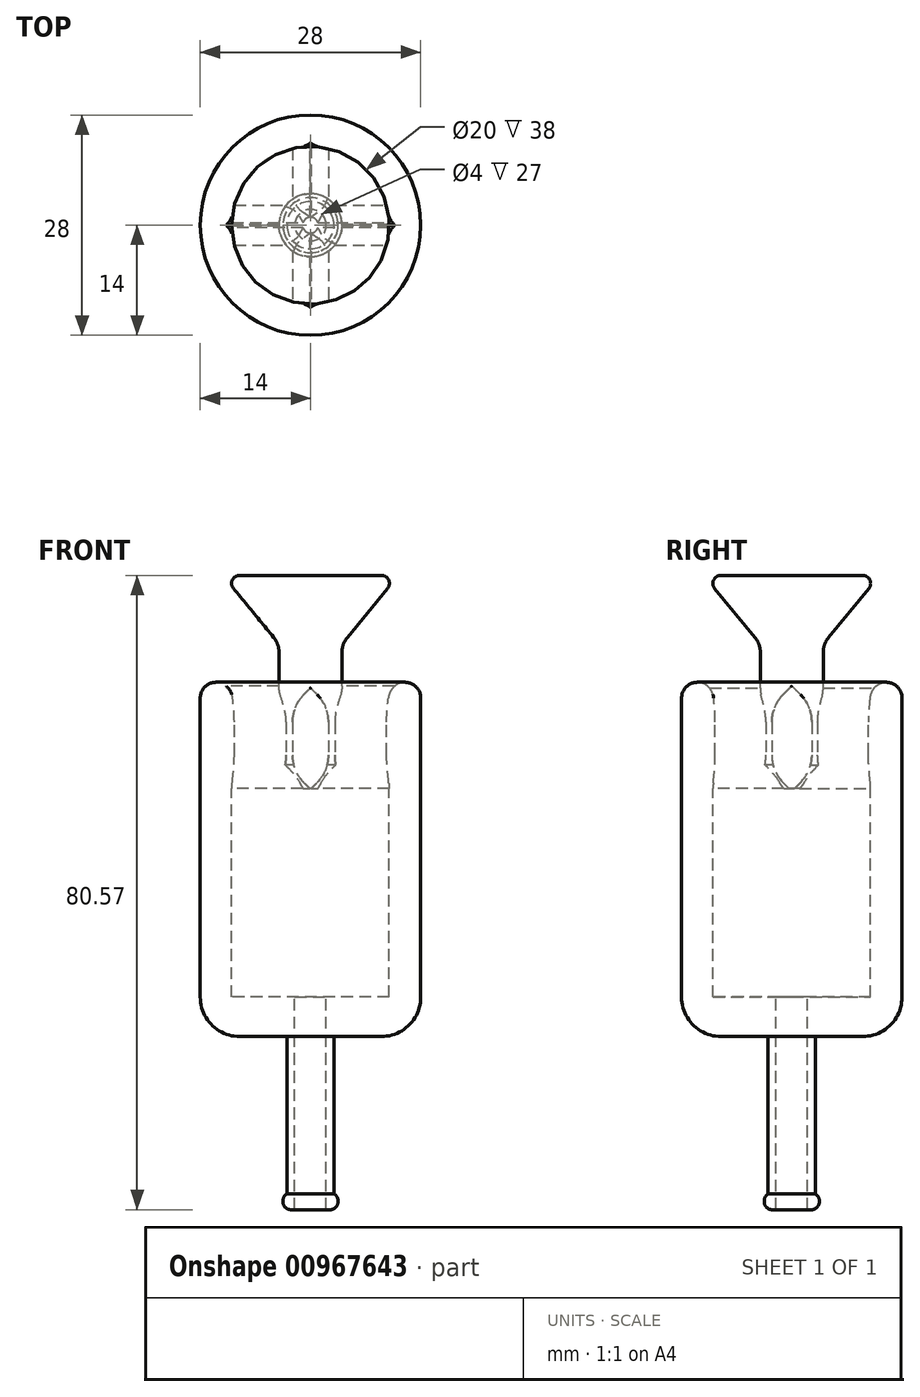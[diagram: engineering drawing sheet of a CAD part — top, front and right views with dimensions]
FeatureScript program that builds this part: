
annotation { "Feature Type Name" : "Feature", "Feature Type Description" : "" }
export const myFeature = defineFeature(function(context is Context, id is Id, definition is map)
    precondition{}
    {
        {
            var Q0;
            Q0=qCreatedBy(makeId("Front.planeOp"),FACE);
            var sketch = newSketch(context, id + "F0", { "sketchPlane" : qUnion([Q0])});
            skLineSegment(sketch, "E0", {"start": v(0, 0) * mm, "end": v(-11.14, 13.57) * mm});
            skLineSegment(sketch, "E1", {"start": v(-11.14, 13.57) * mm, "end": v(0, 13.57) * mm});
            skLineSegment(sketch, "E2", {"start": v(0, 13.57) * mm, "end": v(0, 0) * mm});
            skLineSegment(sketch, "E3", {"start": v(0, 0) * mm, "end": v(-5.28, 0) * mm});
            skLineSegment(sketch, "E4", {"start": v(-5.28, 0) * mm, "end": v(-5.28, -11.56) * mm});
            skLineSegment(sketch, "E5", {"start": v(-5.28, -11.56) * mm, "end": v(0, -11.56) * mm});
            skLineSegment(sketch, "E6", {"start": v(0, -11.56) * mm, "end": v(0, 0) * mm});
            skSolve(sketch);
        }
        {
            var Q0;
            Q0=makeQuery(id+"F0.imprint","IMPRINT",FACE,{"disambiguationData":[TD([[makeQuery(id+"F0.imprint","IMPRINT",EDGE,{"derivedFrom":sQuery(id+"F0.wireOp",EDGE,"E0")}),-1.0]])]});
            var Q1;
            Q1=sQuery(id+"F0.wireOp",EDGE,"E2");
            revolve(context, id + "F1", {"surfaceOperationType" : NewSurfaceOperationType.NEW, "entities" : qUnion([Q0]), "axis" : qUnion([Q1]), "revolveType" : RevolveType.FULL});
        }
        {
            var Q0;
            Q0=qCreatedBy(makeId("Top.planeOp"),FACE);
            var sketch = newSketch(context, id + "F2", { "sketchPlane" : qUnion([Q0])});
            skCircle(sketch, "E7", {"center": v(0, 0) * mm, "radius": 14 * mm});
            skCircle(sketch, "E8", {"center": v(0, 0) * mm, "radius": 10 * mm});
            skCircle(sketch, "E9", {"center": v(0, 0) * mm, "radius": 4 * mm});
            skSolve(sketch);
        }
        {
            var Q0;
            Q0=makeQuery(id+"F2.imprint","IMPRINT",FACE,{"disambiguationData":[TD([[makeQuery(id+"F2.imprint","IMPRINT",EDGE,{"derivedFrom":sQuery(id+"F2.wireOp",EDGE,"E9")}),1.0]])]});
            extrude(context, id + "F3", {"entities" : qUnion([Q0]), "operationType" : NewBodyOperationType.ADD, "endBound" : BoundingType.SYMMETRIC, "oppositeDirection" : true, "depth" : 27 * mm, "offsetDistance" : 25 * mm});
        }
        {
            var Q0;
            Q0=makeQuery(id+"F2.imprint","IMPRINT",FACE,{"disambiguationData":[TD([[makeQuery(id+"F2.imprint","IMPRINT",EDGE,{"derivedFrom":sQuery(id+"F2.wireOp",EDGE,"E7")}),1.0]])]});
            extrude(context, id + "F4", {"entities" : qUnion([Q0]), "depth" : -40 * mm, "offsetDistance" : 25 * mm});
        }
        {
            var Q0;
            Q0=makeQuery(id+"F3.opExtrude","CAP_FACE",FACE,{"disambiguationData":[OSD([sQuery(id+"F2.wireOp",EDGE,"E9")])],"isStart":false});
            var sketch = newSketch(context, id + "F5", { "sketchPlane" : qUnion([Q0])});
            skLineSegment(sketch, "E10.bottom", {"start": v(2.28, -13) * mm, "end": v(-2.28, -13) * mm});
            skLineSegment(sketch, "E10.top", {"start": v(2.28, 13) * mm, "end": v(-2.28, 13) * mm});
            skLineSegment(sketch, "E10.left", {"start": v(2.28, -13) * mm, "end": v(2.28, 13) * mm});
            skLineSegment(sketch, "E10.right", {"start": v(-2.28, -13) * mm, "end": v(-2.28, 13) * mm});
            skPoint(sketch, "E10.middle", {"position": v(0, 0) * mm});
            skLineSegment(sketch, "E11.bottom", {"start": v(-13.08, 2.54) * mm, "end": v(13.08, 2.54) * mm});
            skLineSegment(sketch, "E11.top", {"start": v(-13.08, -2.54) * mm, "end": v(13.08, -2.54) * mm});
            skLineSegment(sketch, "E11.left", {"start": v(-13.08, 2.54) * mm, "end": v(-13.08, -2.54) * mm});
            skLineSegment(sketch, "E11.right", {"start": v(13.08, 2.54) * mm, "end": v(13.08, -2.54) * mm});
            skSolve(sketch);
        }
        {
            var Q0;
            {var subQ0=sQuery(id+"F5.wireOp",EDGE,"E11.left");Q0=makeQuery(id+"F5.imprint","IMPRINT",FACE,{"disambiguationData":[TD([[makeQuery(id+"F5.imprint","IMPRINT",EDGE,{"derivedFrom":subQ0}),1.0]])]});}
            var Q1;
            {var subQ0=sQuery(id+"F5.wireOp",EDGE,"E11.right");Q1=makeQuery(id+"F5.imprint","IMPRINT",FACE,{"disambiguationData":[TD([[makeQuery(id+"F5.imprint","IMPRINT",EDGE,{"derivedFrom":subQ0}),-1.0]])]});}
            var Q2;
            {var subQ0=sQuery(id+"F5.wireOp",EDGE,"E10.top");Q2=makeQuery(id+"F5.imprint","IMPRINT",FACE,{"disambiguationData":[TD([[makeQuery(id+"F5.imprint","IMPRINT",EDGE,{"derivedFrom":subQ0}),1.0]])]});}
            var Q3;
            {var subQ0=sQuery(id+"F5.wireOp",EDGE,"E10.bottom");Q3=makeQuery(id+"F5.imprint","IMPRINT",FACE,{"disambiguationData":[TD([[makeQuery(id+"F5.imprint","IMPRINT",EDGE,{"derivedFrom":subQ0}),-1.0]])]});}
            extrude(context, id + "F6", {"entities" : qUnion([Q0, Q1, Q2, Q3]), "operationType" : NewBodyOperationType.ADD, "depth" : -13 * mm, "offsetDistance" : 25 * mm});
        }
        {
            var Q0;
            {var subQ0=sQuery(id+"F5.wireOp",EDGE,"E11.bottom");Q0=makeQuery(id+"F6.opExtrude","CAP_EDGE",EDGE,{"disambiguationData":[OSD([subQ0]),TDD([makeQuery(id+"F5.imprint","IMPRINT",EDGE,{"disambiguationData":[TD([[makeQuery(id+"F5.imprint","INTERSECT",VERTEX,{"derivedFrom":[subQ0,sQuery(id+"F5.wireOp",EDGE,"E11.left")]}),-1.0]])],"derivedFrom":subQ0})])],"isStart":true});}
            var Q1;
            {var subQ0=sQuery(id+"F5.wireOp",EDGE,"E11.top");Q1=makeQuery(id+"F6.opExtrude","CAP_EDGE",EDGE,{"disambiguationData":[OSD([subQ0]),TDD([makeQuery(id+"F5.imprint","IMPRINT",EDGE,{"disambiguationData":[TD([[makeQuery(id+"F5.imprint","INTERSECT",VERTEX,{"derivedFrom":[subQ0,sQuery(id+"F5.wireOp",EDGE,"E11.right")]}),1.0]])],"derivedFrom":subQ0})])],"isStart":true});}
            var Q2;
            {var subQ0=sQuery(id+"F5.wireOp",EDGE,"E10.left");Q2=makeQuery(id+"F6.opExtrude","CAP_EDGE",EDGE,{"disambiguationData":[OSD([subQ0]),TDD([makeQuery(id+"F5.imprint","IMPRINT",EDGE,{"disambiguationData":[TD([[makeQuery(id+"F5.imprint","INTERSECT",VERTEX,{"derivedFrom":[sQuery(id+"F5.wireOp",EDGE,"E10.top"),subQ0]}),1.0]])],"derivedFrom":subQ0})])],"isStart":true});}
            var Q3;
            {var subQ0=sQuery(id+"F5.wireOp",EDGE,"E10.right");Q3=makeQuery(id+"F6.opExtrude","CAP_EDGE",EDGE,{"disambiguationData":[OSD([subQ0]),TDD([makeQuery(id+"F5.imprint","IMPRINT",EDGE,{"disambiguationData":[TD([[makeQuery(id+"F5.imprint","INTERSECT",VERTEX,{"derivedFrom":[sQuery(id+"F5.wireOp",EDGE,"E10.bottom"),subQ0]}),-1.0]])],"derivedFrom":subQ0})])],"isStart":true});}
            var Q4;
            {var subQ0=sQuery(id+"F5.wireOp",EDGE,"E11.top");Q4=makeQuery(id+"F6.opExtrude","CAP_EDGE",EDGE,{"disambiguationData":[OSD([subQ0]),TDD([makeQuery(id+"F5.imprint","IMPRINT",EDGE,{"disambiguationData":[TD([[makeQuery(id+"F5.imprint","INTERSECT",VERTEX,{"derivedFrom":[subQ0,sQuery(id+"F5.wireOp",EDGE,"E11.left")]}),-1.0]])],"derivedFrom":subQ0})])],"isStart":true});}
            var Q5;
            {var subQ0=sQuery(id+"F5.wireOp",EDGE,"E11.bottom");Q5=makeQuery(id+"F6.opExtrude","CAP_EDGE",EDGE,{"disambiguationData":[OSD([subQ0]),TDD([makeQuery(id+"F5.imprint","IMPRINT",EDGE,{"disambiguationData":[TD([[makeQuery(id+"F5.imprint","INTERSECT",VERTEX,{"derivedFrom":[subQ0,sQuery(id+"F5.wireOp",EDGE,"E11.right")]}),1.0]])],"derivedFrom":subQ0})])],"isStart":true});}
            var Q6;
            {var subQ0=sQuery(id+"F5.wireOp",EDGE,"E10.right");Q6=makeQuery(id+"F6.opExtrude","CAP_EDGE",EDGE,{"disambiguationData":[OSD([subQ0]),TDD([makeQuery(id+"F5.imprint","IMPRINT",EDGE,{"disambiguationData":[TD([[makeQuery(id+"F5.imprint","INTERSECT",VERTEX,{"derivedFrom":[sQuery(id+"F5.wireOp",EDGE,"E10.top"),subQ0]}),1.0]])],"derivedFrom":subQ0})])],"isStart":true});}
            var Q7;
            {var subQ0=sQuery(id+"F5.wireOp",EDGE,"E10.left");Q7=makeQuery(id+"F6.opExtrude","CAP_EDGE",EDGE,{"disambiguationData":[OSD([subQ0]),TDD([makeQuery(id+"F5.imprint","IMPRINT",EDGE,{"disambiguationData":[TD([[makeQuery(id+"F5.imprint","INTERSECT",VERTEX,{"derivedFrom":[sQuery(id+"F5.wireOp",EDGE,"E10.bottom"),subQ0]}),-1.0]])],"derivedFrom":subQ0})])],"isStart":true});}
            chamfer(context, id + "F7", {"entities" : qUnion([Q0, Q1, Q2, Q3, Q4, Q5, Q6, Q7]), "width" : 2.2 * mm, "tangentPropagation" : true});
        }
        {
            var Q0;
            {var subQ0=sQuery(id+"F5.wireOp",EDGE,"E11.bottom");Q0=makeQuery(id+"F6.opExtrude","CAP_EDGE",EDGE,{"disambiguationData":[OSD([subQ0]),TDD([makeQuery(id+"F5.imprint","IMPRINT",EDGE,{"disambiguationData":[TD([[makeQuery(id+"F5.imprint","INTERSECT",VERTEX,{"derivedFrom":[subQ0,sQuery(id+"F5.wireOp",EDGE,"E11.left")]}),-1.0]])],"derivedFrom":subQ0})])],"isStart":false});}
            var Q1;
            {var subQ0=sQuery(id+"F5.wireOp",EDGE,"E11.top");Q1=makeQuery(id+"F6.opExtrude","CAP_EDGE",EDGE,{"disambiguationData":[OSD([subQ0]),TDD([makeQuery(id+"F5.imprint","IMPRINT",EDGE,{"disambiguationData":[TD([[makeQuery(id+"F5.imprint","INTERSECT",VERTEX,{"derivedFrom":[subQ0,sQuery(id+"F5.wireOp",EDGE,"E11.left")]}),-1.0]])],"derivedFrom":subQ0})])],"isStart":false});}
            var Q2;
            {var subQ0=sQuery(id+"F5.wireOp",EDGE,"E10.right");Q2=makeQuery(id+"F6.opExtrude","CAP_EDGE",EDGE,{"disambiguationData":[OSD([subQ0]),TDD([makeQuery(id+"F5.imprint","IMPRINT",EDGE,{"disambiguationData":[TD([[makeQuery(id+"F5.imprint","INTERSECT",VERTEX,{"derivedFrom":[sQuery(id+"F5.wireOp",EDGE,"E10.bottom"),subQ0]}),-1.0]])],"derivedFrom":subQ0})])],"isStart":false});}
            var Q3;
            {var subQ0=sQuery(id+"F5.wireOp",EDGE,"E10.left");Q3=makeQuery(id+"F6.opExtrude","CAP_EDGE",EDGE,{"disambiguationData":[OSD([subQ0]),TDD([makeQuery(id+"F5.imprint","IMPRINT",EDGE,{"disambiguationData":[TD([[makeQuery(id+"F5.imprint","INTERSECT",VERTEX,{"derivedFrom":[sQuery(id+"F5.wireOp",EDGE,"E10.bottom"),subQ0]}),-1.0]])],"derivedFrom":subQ0})])],"isStart":false});}
            var Q4;
            {var subQ0=sQuery(id+"F5.wireOp",EDGE,"E11.bottom");Q4=makeQuery(id+"F6.opExtrude","CAP_EDGE",EDGE,{"disambiguationData":[OSD([subQ0]),TDD([makeQuery(id+"F5.imprint","IMPRINT",EDGE,{"disambiguationData":[TD([[makeQuery(id+"F5.imprint","INTERSECT",VERTEX,{"derivedFrom":[subQ0,sQuery(id+"F5.wireOp",EDGE,"E11.right")]}),1.0]])],"derivedFrom":subQ0})])],"isStart":false});}
            var Q5;
            {var subQ0=sQuery(id+"F5.wireOp",EDGE,"E11.top");Q5=makeQuery(id+"F6.opExtrude","CAP_EDGE",EDGE,{"disambiguationData":[OSD([subQ0]),TDD([makeQuery(id+"F5.imprint","IMPRINT",EDGE,{"disambiguationData":[TD([[makeQuery(id+"F5.imprint","INTERSECT",VERTEX,{"derivedFrom":[subQ0,sQuery(id+"F5.wireOp",EDGE,"E11.right")]}),1.0]])],"derivedFrom":subQ0})])],"isStart":false});}
            var Q6;
            {var subQ0=sQuery(id+"F5.wireOp",EDGE,"E10.left");Q6=makeQuery(id+"F6.opExtrude","CAP_EDGE",EDGE,{"disambiguationData":[OSD([subQ0]),TDD([makeQuery(id+"F5.imprint","IMPRINT",EDGE,{"disambiguationData":[TD([[makeQuery(id+"F5.imprint","INTERSECT",VERTEX,{"derivedFrom":[sQuery(id+"F5.wireOp",EDGE,"E10.top"),subQ0]}),1.0]])],"derivedFrom":subQ0})])],"isStart":false});}
            var Q7;
            {var subQ0=sQuery(id+"F5.wireOp",EDGE,"E10.right");Q7=makeQuery(id+"F6.opExtrude","CAP_EDGE",EDGE,{"disambiguationData":[OSD([subQ0]),TDD([makeQuery(id+"F5.imprint","IMPRINT",EDGE,{"disambiguationData":[TD([[makeQuery(id+"F5.imprint","INTERSECT",VERTEX,{"derivedFrom":[sQuery(id+"F5.wireOp",EDGE,"E10.top"),subQ0]}),1.0]])],"derivedFrom":subQ0})])],"isStart":false});}
            chamfer(context, id + "F8", {"entities" : qUnion([Q0, Q1, Q2, Q3, Q4, Q5, Q6, Q7]), "width" : 2.5 * mm, "tangentPropagation" : true});
        }
        {
            var Q0;
            {var subQ0=sQuery(id+"F5.wireOp",EDGE,"E10.right");var subQ1=makeQuery(id+"F5.imprint","IMPRINT",EDGE,{"disambiguationData":[TD([[makeQuery(id+"F5.imprint","INTERSECT",VERTEX,{"derivedFrom":[sQuery(id+"F5.wireOp",EDGE,"E10.top"),subQ0]}),1.0]])],"derivedFrom":subQ0});Q0=makeQuery(id+"F7.opChamfer","BLEND_EDGE",EDGE,{"blendedFrom":[makeQuery(id+"F6.opExtrude","CAP_EDGE",EDGE,{"disambiguationData":[OSD([subQ0]),TDD([subQ1])],"isStart":true}),makeQuery(id+"F6.opExtrude","SWEPT_FACE",FACE,{"disambiguationData":[OSD([subQ0]),TDD([subQ1])]})],"blendedInto":[makeQuery(id+"F6.opExtrude","SWEPT_FACE",FACE,{"disambiguationData":[OSD([subQ0]),TDD([subQ1])]})]});}
            var Q1;
            {var subQ0=sQuery(id+"F5.wireOp",EDGE,"E10.left");var subQ1=makeQuery(id+"F5.imprint","IMPRINT",EDGE,{"disambiguationData":[TD([[makeQuery(id+"F5.imprint","INTERSECT",VERTEX,{"derivedFrom":[sQuery(id+"F5.wireOp",EDGE,"E10.top"),subQ0]}),1.0]])],"derivedFrom":subQ0});Q1=makeQuery(id+"F7.opChamfer","BLEND_EDGE",EDGE,{"blendedFrom":[makeQuery(id+"F6.opExtrude","CAP_EDGE",EDGE,{"disambiguationData":[OSD([subQ0]),TDD([subQ1])],"isStart":true}),makeQuery(id+"F6.opExtrude","SWEPT_FACE",FACE,{"disambiguationData":[OSD([subQ0]),TDD([subQ1])]})],"blendedInto":[makeQuery(id+"F6.opExtrude","SWEPT_FACE",FACE,{"disambiguationData":[OSD([subQ0]),TDD([subQ1])]})]});}
            var Q2;
            {var subQ0=sQuery(id+"F5.wireOp",EDGE,"E11.bottom");var subQ1=makeQuery(id+"F5.imprint","IMPRINT",EDGE,{"disambiguationData":[TD([[makeQuery(id+"F5.imprint","INTERSECT",VERTEX,{"derivedFrom":[subQ0,sQuery(id+"F5.wireOp",EDGE,"E11.right")]}),1.0]])],"derivedFrom":subQ0});Q2=makeQuery(id+"F7.opChamfer","BLEND_EDGE",EDGE,{"blendedFrom":[makeQuery(id+"F6.opExtrude","CAP_EDGE",EDGE,{"disambiguationData":[OSD([subQ0]),TDD([subQ1])],"isStart":true}),makeQuery(id+"F6.opExtrude","SWEPT_FACE",FACE,{"disambiguationData":[OSD([subQ0]),TDD([subQ1])]})],"blendedInto":[makeQuery(id+"F6.opExtrude","SWEPT_FACE",FACE,{"disambiguationData":[OSD([subQ0]),TDD([subQ1])]})]});}
            var Q3;
            {var subQ0=sQuery(id+"F5.wireOp",EDGE,"E11.bottom");var subQ1=makeQuery(id+"F5.imprint","IMPRINT",EDGE,{"disambiguationData":[TD([[makeQuery(id+"F5.imprint","INTERSECT",VERTEX,{"derivedFrom":[subQ0,sQuery(id+"F5.wireOp",EDGE,"E11.left")]}),-1.0]])],"derivedFrom":subQ0});Q3=makeQuery(id+"F7.opChamfer","BLEND_EDGE",EDGE,{"blendedFrom":[makeQuery(id+"F6.opExtrude","CAP_EDGE",EDGE,{"disambiguationData":[OSD([subQ0]),TDD([subQ1])],"isStart":true}),makeQuery(id+"F6.opExtrude","SWEPT_FACE",FACE,{"disambiguationData":[OSD([subQ0]),TDD([subQ1])]})],"blendedInto":[makeQuery(id+"F6.opExtrude","SWEPT_FACE",FACE,{"disambiguationData":[OSD([subQ0]),TDD([subQ1])]})]});}
            var Q4;
            {var subQ0=sQuery(id+"F5.wireOp",EDGE,"E11.top");var subQ1=makeQuery(id+"F5.imprint","IMPRINT",EDGE,{"disambiguationData":[TD([[makeQuery(id+"F5.imprint","INTERSECT",VERTEX,{"derivedFrom":[subQ0,sQuery(id+"F5.wireOp",EDGE,"E11.left")]}),-1.0]])],"derivedFrom":subQ0});Q4=makeQuery(id+"F7.opChamfer","BLEND_EDGE",EDGE,{"blendedFrom":[makeQuery(id+"F6.opExtrude","CAP_EDGE",EDGE,{"disambiguationData":[OSD([subQ0]),TDD([subQ1])],"isStart":true}),makeQuery(id+"F6.opExtrude","SWEPT_FACE",FACE,{"disambiguationData":[OSD([subQ0]),TDD([subQ1])]})],"blendedInto":[makeQuery(id+"F6.opExtrude","SWEPT_FACE",FACE,{"disambiguationData":[OSD([subQ0]),TDD([subQ1])]})]});}
            var Q5;
            {var subQ0=sQuery(id+"F5.wireOp",EDGE,"E11.top");var subQ1=makeQuery(id+"F5.imprint","IMPRINT",EDGE,{"disambiguationData":[TD([[makeQuery(id+"F5.imprint","INTERSECT",VERTEX,{"derivedFrom":[subQ0,sQuery(id+"F5.wireOp",EDGE,"E11.right")]}),1.0]])],"derivedFrom":subQ0});Q5=makeQuery(id+"F7.opChamfer","BLEND_EDGE",EDGE,{"blendedFrom":[makeQuery(id+"F6.opExtrude","CAP_EDGE",EDGE,{"disambiguationData":[OSD([subQ0]),TDD([subQ1])],"isStart":true}),makeQuery(id+"F6.opExtrude","SWEPT_FACE",FACE,{"disambiguationData":[OSD([subQ0]),TDD([subQ1])]})],"blendedInto":[makeQuery(id+"F6.opExtrude","SWEPT_FACE",FACE,{"disambiguationData":[OSD([subQ0]),TDD([subQ1])]})]});}
            var Q6;
            {var subQ0=sQuery(id+"F5.wireOp",EDGE,"E10.right");var subQ1=makeQuery(id+"F5.imprint","IMPRINT",EDGE,{"disambiguationData":[TD([[makeQuery(id+"F5.imprint","INTERSECT",VERTEX,{"derivedFrom":[sQuery(id+"F5.wireOp",EDGE,"E10.bottom"),subQ0]}),-1.0]])],"derivedFrom":subQ0});Q6=makeQuery(id+"F7.opChamfer","BLEND_EDGE",EDGE,{"blendedFrom":[makeQuery(id+"F6.opExtrude","CAP_EDGE",EDGE,{"disambiguationData":[OSD([subQ0]),TDD([subQ1])],"isStart":true}),makeQuery(id+"F6.opExtrude","SWEPT_FACE",FACE,{"disambiguationData":[OSD([subQ0]),TDD([subQ1])]})],"blendedInto":[makeQuery(id+"F6.opExtrude","SWEPT_FACE",FACE,{"disambiguationData":[OSD([subQ0]),TDD([subQ1])]})]});}
            var Q7;
            {var subQ0=sQuery(id+"F5.wireOp",EDGE,"E10.left");var subQ1=makeQuery(id+"F5.imprint","IMPRINT",EDGE,{"disambiguationData":[TD([[makeQuery(id+"F5.imprint","INTERSECT",VERTEX,{"derivedFrom":[sQuery(id+"F5.wireOp",EDGE,"E10.bottom"),subQ0]}),-1.0]])],"derivedFrom":subQ0});Q7=makeQuery(id+"F7.opChamfer","BLEND_EDGE",EDGE,{"blendedFrom":[makeQuery(id+"F6.opExtrude","CAP_EDGE",EDGE,{"disambiguationData":[OSD([subQ0]),TDD([subQ1])],"isStart":true}),makeQuery(id+"F6.opExtrude","SWEPT_FACE",FACE,{"disambiguationData":[OSD([subQ0]),TDD([subQ1])]})],"blendedInto":[makeQuery(id+"F6.opExtrude","SWEPT_FACE",FACE,{"disambiguationData":[OSD([subQ0]),TDD([subQ1])]})]});}
            var Q8;
            {var subQ0=sQuery(id+"F5.wireOp",EDGE,"E10.right");var subQ1=makeQuery(id+"F5.imprint","IMPRINT",EDGE,{"disambiguationData":[TD([[makeQuery(id+"F5.imprint","INTERSECT",VERTEX,{"derivedFrom":[sQuery(id+"F5.wireOp",EDGE,"E10.top"),subQ0]}),1.0]])],"derivedFrom":subQ0});Q8=makeQuery(id+"F8.opChamfer","BLEND_EDGE",EDGE,{"blendedFrom":[makeQuery(id+"F6.opExtrude","CAP_EDGE",EDGE,{"disambiguationData":[OSD([subQ0]),TDD([subQ1])],"isStart":false}),makeQuery(id+"F6.opExtrude","SWEPT_FACE",FACE,{"disambiguationData":[OSD([subQ0]),TDD([subQ1])]})],"blendedInto":[makeQuery(id+"F6.opExtrude","SWEPT_FACE",FACE,{"disambiguationData":[OSD([subQ0]),TDD([subQ1])]})]});}
            var Q9;
            {var subQ0=sQuery(id+"F5.wireOp",EDGE,"E11.bottom");var subQ1=makeQuery(id+"F5.imprint","IMPRINT",EDGE,{"disambiguationData":[TD([[makeQuery(id+"F5.imprint","INTERSECT",VERTEX,{"derivedFrom":[subQ0,sQuery(id+"F5.wireOp",EDGE,"E11.left")]}),-1.0]])],"derivedFrom":subQ0});Q9=makeQuery(id+"F8.opChamfer","BLEND_EDGE",EDGE,{"blendedFrom":[makeQuery(id+"F6.opExtrude","CAP_EDGE",EDGE,{"disambiguationData":[OSD([subQ0]),TDD([subQ1])],"isStart":false}),makeQuery(id+"F6.opExtrude","SWEPT_FACE",FACE,{"disambiguationData":[OSD([subQ0]),TDD([subQ1])]})],"blendedInto":[makeQuery(id+"F6.opExtrude","SWEPT_FACE",FACE,{"disambiguationData":[OSD([subQ0]),TDD([subQ1])]})]});}
            var Q10;
            {var subQ0=sQuery(id+"F5.wireOp",EDGE,"E11.bottom");var subQ1=makeQuery(id+"F5.imprint","IMPRINT",EDGE,{"disambiguationData":[TD([[makeQuery(id+"F5.imprint","INTERSECT",VERTEX,{"derivedFrom":[subQ0,sQuery(id+"F5.wireOp",EDGE,"E11.right")]}),1.0]])],"derivedFrom":subQ0});Q10=makeQuery(id+"F8.opChamfer","BLEND_EDGE",EDGE,{"blendedFrom":[makeQuery(id+"F6.opExtrude","CAP_EDGE",EDGE,{"disambiguationData":[OSD([subQ0]),TDD([subQ1])],"isStart":false}),makeQuery(id+"F6.opExtrude","SWEPT_FACE",FACE,{"disambiguationData":[OSD([subQ0]),TDD([subQ1])]})],"blendedInto":[makeQuery(id+"F6.opExtrude","SWEPT_FACE",FACE,{"disambiguationData":[OSD([subQ0]),TDD([subQ1])]})]});}
            var Q11;
            {var subQ0=sQuery(id+"F5.wireOp",EDGE,"E10.left");var subQ1=makeQuery(id+"F5.imprint","IMPRINT",EDGE,{"disambiguationData":[TD([[makeQuery(id+"F5.imprint","INTERSECT",VERTEX,{"derivedFrom":[sQuery(id+"F5.wireOp",EDGE,"E10.top"),subQ0]}),1.0]])],"derivedFrom":subQ0});Q11=makeQuery(id+"F8.opChamfer","BLEND_EDGE",EDGE,{"blendedFrom":[makeQuery(id+"F6.opExtrude","CAP_EDGE",EDGE,{"disambiguationData":[OSD([subQ0]),TDD([subQ1])],"isStart":false}),makeQuery(id+"F6.opExtrude","SWEPT_FACE",FACE,{"disambiguationData":[OSD([subQ0]),TDD([subQ1])]})],"blendedInto":[makeQuery(id+"F6.opExtrude","SWEPT_FACE",FACE,{"disambiguationData":[OSD([subQ0]),TDD([subQ1])]})]});}
            var Q12;
            {var subQ0=sQuery(id+"F5.wireOp",EDGE,"E11.top");var subQ1=makeQuery(id+"F5.imprint","IMPRINT",EDGE,{"disambiguationData":[TD([[makeQuery(id+"F5.imprint","INTERSECT",VERTEX,{"derivedFrom":[subQ0,sQuery(id+"F5.wireOp",EDGE,"E11.right")]}),1.0]])],"derivedFrom":subQ0});Q12=makeQuery(id+"F8.opChamfer","BLEND_EDGE",EDGE,{"blendedFrom":[makeQuery(id+"F6.opExtrude","CAP_EDGE",EDGE,{"disambiguationData":[OSD([subQ0]),TDD([subQ1])],"isStart":false}),makeQuery(id+"F6.opExtrude","SWEPT_FACE",FACE,{"disambiguationData":[OSD([subQ0]),TDD([subQ1])]})],"blendedInto":[makeQuery(id+"F6.opExtrude","SWEPT_FACE",FACE,{"disambiguationData":[OSD([subQ0]),TDD([subQ1])]})]});}
            var Q13;
            {var subQ0=sQuery(id+"F5.wireOp",EDGE,"E11.top");var subQ1=makeQuery(id+"F5.imprint","IMPRINT",EDGE,{"disambiguationData":[TD([[makeQuery(id+"F5.imprint","INTERSECT",VERTEX,{"derivedFrom":[subQ0,sQuery(id+"F5.wireOp",EDGE,"E11.left")]}),-1.0]])],"derivedFrom":subQ0});Q13=makeQuery(id+"F8.opChamfer","BLEND_EDGE",EDGE,{"blendedFrom":[makeQuery(id+"F6.opExtrude","CAP_EDGE",EDGE,{"disambiguationData":[OSD([subQ0]),TDD([subQ1])],"isStart":false}),makeQuery(id+"F6.opExtrude","SWEPT_FACE",FACE,{"disambiguationData":[OSD([subQ0]),TDD([subQ1])]})],"blendedInto":[makeQuery(id+"F6.opExtrude","SWEPT_FACE",FACE,{"disambiguationData":[OSD([subQ0]),TDD([subQ1])]})]});}
            var Q14;
            {var subQ0=sQuery(id+"F5.wireOp",EDGE,"E10.left");var subQ1=makeQuery(id+"F5.imprint","IMPRINT",EDGE,{"disambiguationData":[TD([[makeQuery(id+"F5.imprint","INTERSECT",VERTEX,{"derivedFrom":[sQuery(id+"F5.wireOp",EDGE,"E10.bottom"),subQ0]}),-1.0]])],"derivedFrom":subQ0});Q14=makeQuery(id+"F8.opChamfer","BLEND_EDGE",EDGE,{"blendedFrom":[makeQuery(id+"F6.opExtrude","CAP_EDGE",EDGE,{"disambiguationData":[OSD([subQ0]),TDD([subQ1])],"isStart":false}),makeQuery(id+"F6.opExtrude","SWEPT_FACE",FACE,{"disambiguationData":[OSD([subQ0]),TDD([subQ1])]})],"blendedInto":[makeQuery(id+"F6.opExtrude","SWEPT_FACE",FACE,{"disambiguationData":[OSD([subQ0]),TDD([subQ1])]})]});}
            var Q15;
            {var subQ0=sQuery(id+"F5.wireOp",EDGE,"E10.right");var subQ1=makeQuery(id+"F5.imprint","IMPRINT",EDGE,{"disambiguationData":[TD([[makeQuery(id+"F5.imprint","INTERSECT",VERTEX,{"derivedFrom":[sQuery(id+"F5.wireOp",EDGE,"E10.bottom"),subQ0]}),-1.0]])],"derivedFrom":subQ0});Q15=makeQuery(id+"F8.opChamfer","BLEND_EDGE",EDGE,{"blendedFrom":[makeQuery(id+"F6.opExtrude","CAP_EDGE",EDGE,{"disambiguationData":[OSD([subQ0]),TDD([subQ1])],"isStart":false}),makeQuery(id+"F6.opExtrude","SWEPT_FACE",FACE,{"disambiguationData":[OSD([subQ0]),TDD([subQ1])]})],"blendedInto":[makeQuery(id+"F6.opExtrude","SWEPT_FACE",FACE,{"disambiguationData":[OSD([subQ0]),TDD([subQ1])]})]});}
            fillet(context, id + "F9", {"entities" : qUnion([Q0, Q1, Q2, Q3, Q4, Q5, Q6, Q7, Q8, Q9, Q10, Q11, Q12, Q13, Q14, Q15]), "radius" : 5 * mm, "tangentPropagation" : true, "allowEdgeOverflow" : false});
        }
        {
            var Q0;
            {var subQ0=sQuery(id+"F5.wireOp",EDGE,"E10.right");var subQ2=sQuery(id+"F5.wireOp",EDGE,"E10.top");var subQ3=sQuery(id+"F2.wireOp",EDGE,"E9");var subQ4=makeQuery(id+"F3.opExtrude","CAP_EDGE",EDGE,{"disambiguationData":[OSD([subQ3])],"isStart":false});Q0=makeQuery(id+"F6.boolean.opBoolean","SPLIT",EDGE,{"disambiguationData":[TD([makeQuery(id+"F6.opExtrude","SWEPT_FACE",FACE,{"disambiguationData":[OSD([subQ0]),TDD([makeQuery(id+"F5.imprint","IMPRINT",EDGE,{"disambiguationData":[TD([[makeQuery(id+"F5.imprint","INTERSECT",VERTEX,{"derivedFrom":[subQ2,subQ0]}),1.0]])],"derivedFrom":subQ0})])]})])],"derivedFrom":subQ4});}
            var Q1;
            {var subQ0=sQuery(id+"F5.wireOp",EDGE,"E10.right");var subQ2=sQuery(id+"F2.wireOp",EDGE,"E9");var subQ3=sQuery(id+"F5.wireOp",EDGE,"E10.bottom");var subQ4=makeQuery(id+"F3.opExtrude","CAP_EDGE",EDGE,{"disambiguationData":[OSD([subQ2])],"isStart":false});Q1=makeQuery(id+"F6.boolean.opBoolean","SPLIT",EDGE,{"disambiguationData":[TD([makeQuery(id+"F6.opExtrude","SWEPT_FACE",FACE,{"disambiguationData":[OSD([subQ0]),TDD([makeQuery(id+"F5.imprint","IMPRINT",EDGE,{"disambiguationData":[TD([[makeQuery(id+"F5.imprint","INTERSECT",VERTEX,{"derivedFrom":[subQ3,subQ0]}),-1.0]])],"derivedFrom":subQ0})])]})])],"derivedFrom":subQ4});}
            var Q2;
            {var subQ1=sQuery(id+"F5.wireOp",EDGE,"E10.left");var subQ2=sQuery(id+"F2.wireOp",EDGE,"E9");var subQ3=sQuery(id+"F5.wireOp",EDGE,"E10.bottom");var subQ4=makeQuery(id+"F3.opExtrude","CAP_EDGE",EDGE,{"disambiguationData":[OSD([subQ2])],"isStart":false});Q2=makeQuery(id+"F6.boolean.opBoolean","SPLIT",EDGE,{"disambiguationData":[TD([makeQuery(id+"F6.opExtrude","SWEPT_FACE",FACE,{"disambiguationData":[OSD([subQ1]),TDD([makeQuery(id+"F5.imprint","IMPRINT",EDGE,{"disambiguationData":[TD([[makeQuery(id+"F5.imprint","INTERSECT",VERTEX,{"derivedFrom":[subQ3,subQ1]}),-1.0]])],"derivedFrom":subQ1})])]})])],"derivedFrom":subQ4});}
            var Q3;
            {var subQ1=sQuery(id+"F5.wireOp",EDGE,"E10.left");var subQ2=sQuery(id+"F5.wireOp",EDGE,"E10.top");var subQ3=sQuery(id+"F2.wireOp",EDGE,"E9");var subQ6=makeQuery(id+"F3.opExtrude","CAP_EDGE",EDGE,{"disambiguationData":[OSD([subQ3])],"isStart":false});Q3=makeQuery(id+"F6.boolean.opBoolean","SPLIT",EDGE,{"disambiguationData":[TD([makeQuery(id+"F6.opExtrude","SWEPT_FACE",FACE,{"disambiguationData":[OSD([subQ1]),TDD([makeQuery(id+"F5.imprint","IMPRINT",EDGE,{"disambiguationData":[TD([[makeQuery(id+"F5.imprint","INTERSECT",VERTEX,{"derivedFrom":[subQ2,subQ1]}),1.0]])],"derivedFrom":subQ1})])]})])],"derivedFrom":subQ6});}
            chamfer(context, id + "F10", {"entities" : qUnion([Q0, Q1, Q2, Q3]), "width" : 3 * mm, "tangentPropagation" : true});
        }
        {
            var Q0;
            Q0=makeQuery(id+"F1.opRevolve","SWEPT_EDGE",EDGE,{"disambiguationData":[OSD([sQuery(id+"F0.wireOp",EDGE,"E0"),sQuery(id+"F0.wireOp",EDGE,"E1")])]});
            fillet(context, id + "F11", {"entities" : qUnion([Q0]), "radius" : 1 * mm, "tangentPropagation" : true, "allowEdgeOverflow" : false});
        }
        {
            var Q0;
            Q0=makeQuery(id+"F3.boolean.opBoolean","INTERSECT",EDGE,{"derivedFrom":[makeQuery(id+"F1.opRevolve","SWEPT_FACE",FACE,{"disambiguationData":[OSD([sQuery(id+"F0.wireOp",EDGE,"E0")])]}),makeQuery(id+"F3.opExtrude","SWEPT_FACE",FACE,{"disambiguationData":[OSD([sQuery(id+"F2.wireOp",EDGE,"E9")])]})]});
            fillet(context, id + "F12", {"entities" : qUnion([Q0]), "radius" : 3 * mm, "tangentPropagation" : true, "allowEdgeOverflow" : false});
        }
        {
            var Q0;
            Q0=makeQuery(id+"F4.opExtrude","CAP_EDGE",EDGE,{"disambiguationData":[OSD([sQuery(id+"F2.wireOp",EDGE,"E7")])],"isStart":true});
            var Q1;
            Q1=makeQuery(id+"F4.opExtrude","CAP_EDGE",EDGE,{"disambiguationData":[OSD([sQuery(id+"F2.wireOp",EDGE,"E8")])],"isStart":true});
            fillet(context, id + "F13", {"entities" : qUnion([Q0, Q1]), "radius" : 2 * mm, "tangentPropagation" : true, "allowEdgeOverflow" : false});
        }
        {
            var Q0;
            Q0=makeQuery(id+"F4.opExtrude","CAP_FACE",FACE,{"disambiguationData":[OSD([sQuery(id+"F2.wireOp",EDGE,"E7"),sQuery(id+"F2.wireOp",EDGE,"E8")])],"isStart":false});
            var sketch = newSketch(context, id + "F14", { "sketchPlane" : qUnion([Q0])});
            skCircle(sketch, "E12", {"center": v(0, 0) * mm, "radius": 14 * mm});
            skCircle(sketch, "E13", {"center": v(0, 0) * mm, "radius": 3 * mm});
            skCircle(sketch, "E14", {"center": v(0, 0) * mm, "radius": 2 * mm});
            skSolve(sketch);
        }
        {
            var Q0;
            Q0=makeQuery(id+"F14.imprint","IMPRINT",FACE,{"disambiguationData":[TD([[makeQuery(id+"F14.imprint","IMPRINT",EDGE,{"derivedFrom":sQuery(id+"F14.wireOp",EDGE,"E12")}),-1.0]])]});
            var Q1;
            Q1=makeQuery(id+"F14.imprint","IMPRINT",FACE,{"disambiguationData":[TD([[makeQuery(id+"F14.imprint","IMPRINT",EDGE,{"derivedFrom":sQuery(id+"F14.wireOp",EDGE,"E13")}),-1.0]])]});
            extrude(context, id + "F15", {"entities" : qUnion([Q0, Q1]), "operationType" : NewBodyOperationType.ADD, "depth" : 5 * mm, "offsetDistance" : 25 * mm});
        }
        {
            var Q0;
            Q0=makeQuery(id+"F14.imprint","IMPRINT",FACE,{"disambiguationData":[TD([[makeQuery(id+"F14.imprint","IMPRINT",EDGE,{"derivedFrom":sQuery(id+"F14.wireOp",EDGE,"E13")}),1.0]])]});
            extrude(context, id + "F16", {"entities" : qUnion([Q0]), "operationType" : NewBodyOperationType.ADD, "depth" : 25 * mm, "offsetDistance" : 25 * mm});
        }
        {
            var Q0;
            Q0=makeQuery(id+"F16.opExtrude","CAP_FACE",FACE,{"disambiguationData":[OSD([sQuery(id+"F14.wireOp",EDGE,"E13"),sQuery(id+"F14.wireOp",EDGE,"E14")])],"isStart":false});
            var sketch = newSketch(context, id + "F17", { "sketchPlane" : qUnion([Q0])});
            skCircle(sketch, "E15", {"center": v(0, 0) * mm, "radius": 3.5 * mm});
            skCircle(sketch, "E16", {"center": v(0, 0) * mm, "radius": 2 * mm});
            skSolve(sketch);
        }
        {
            var Q0;
            Q0=makeQuery(id+"F17.imprint","IMPRINT",FACE,{"disambiguationData":[TD([[makeQuery(id+"F17.imprint","IMPRINT",EDGE,{"derivedFrom":sQuery(id+"F17.wireOp",EDGE,"E15")}),1.0]])]});
            var Q1;
            Q1=makeQuery(id+"F17.imprint","IMPRINT",FACE,{"disambiguationData":[TD([[makeQuery(id+"F17.imprint","IMPRINT",EDGE,{"derivedFrom":sQuery(id+"F17.wireOp",EDGE,"E16")}),-1.0]])]});
            extrude(context, id + "F18", {"entities" : qUnion([Q0, Q1]), "operationType" : NewBodyOperationType.ADD, "depth" : 2 * mm, "offsetDistance" : 25 * mm});
        }
        {
            var Q0;
            Q0=makeQuery(id+"F18.opExtrude","CAP_EDGE",EDGE,{"disambiguationData":[OSD([sQuery(id+"F17.wireOp",EDGE,"E15")])],"isStart":false});
            var Q1;
            Q1=makeQuery(id+"F18.opExtrude","CAP_EDGE",EDGE,{"disambiguationData":[OSD([sQuery(id+"F17.wireOp",EDGE,"E15")])],"isStart":true});
            fillet(context, id + "F19", {"entities" : qUnion([Q0, Q1]), "radius" : 1 * mm, "tangentPropagation" : true, "allowEdgeOverflow" : false});
        }
        {
            var Q0;
            Q0=makeQuery(id+"F15.opExtrude","CAP_EDGE",EDGE,{"disambiguationData":[OSD([sQuery(id+"F14.wireOp",EDGE,"E12")])],"isStart":false});
            fillet(context, id + "F20", {"entities" : qUnion([Q0]), "radius" : 5 * mm, "tangentPropagation" : true, "allowEdgeOverflow" : false});
        }
    });
